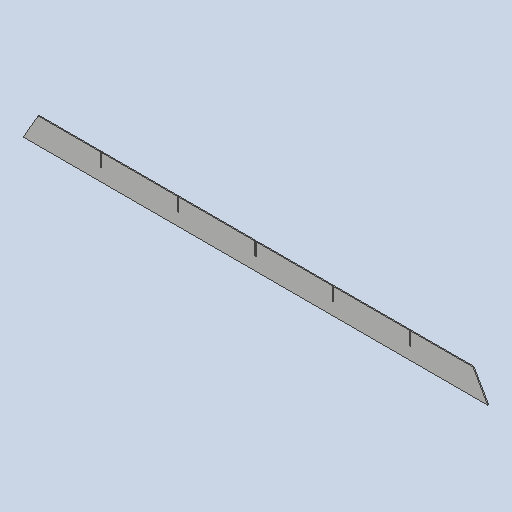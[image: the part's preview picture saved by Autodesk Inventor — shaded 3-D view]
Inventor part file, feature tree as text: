
AUTODESK INVENTOR PART (.ipt)
format: ipt  version: 2025 (Build 290162010, 162A)  size: 323,072 bytes
history: native  units: mm
features: other x3, sketch x2, sheet_metal_op x1, extrude x1, pattern_linear x1
ambient origin geometry x8: Origin, YZ Plane, XZ Plane, XY Plane, X Axis, Y Axis, Z Axis, Center Point
bodies: Solid1 (feature_tree)
feature tree (8):
  other  "MSC 203 GRID"
  sheet_metal_op  "Face1"
  extrude  "Extrusion1"  Depth=80.0mm
  pattern_linear  "Rectangular Pattern1"  Spacing1=120.0deg  [1 undecoded]
  sketch  "Sketch1"  dims[d0=80.0mm d1=1800.0mm]
  other  "Plate1"
  sketch  "Sketch2"  dims[d2=3.0mm d3=120.0deg d6=674.96mm d7=120.0deg d8=674.96mm d9=3.2mm d10=41.0mm d11=0.0mm d12=0.0mm d13=50.0mm d15=240.0mm]
  other  "Definition1"
note: 1 required parameter value undecoded (feature->parameter linkage not recoverable at this tier; creation-order binding heuristic only, values carry confidence <= 0.55)
